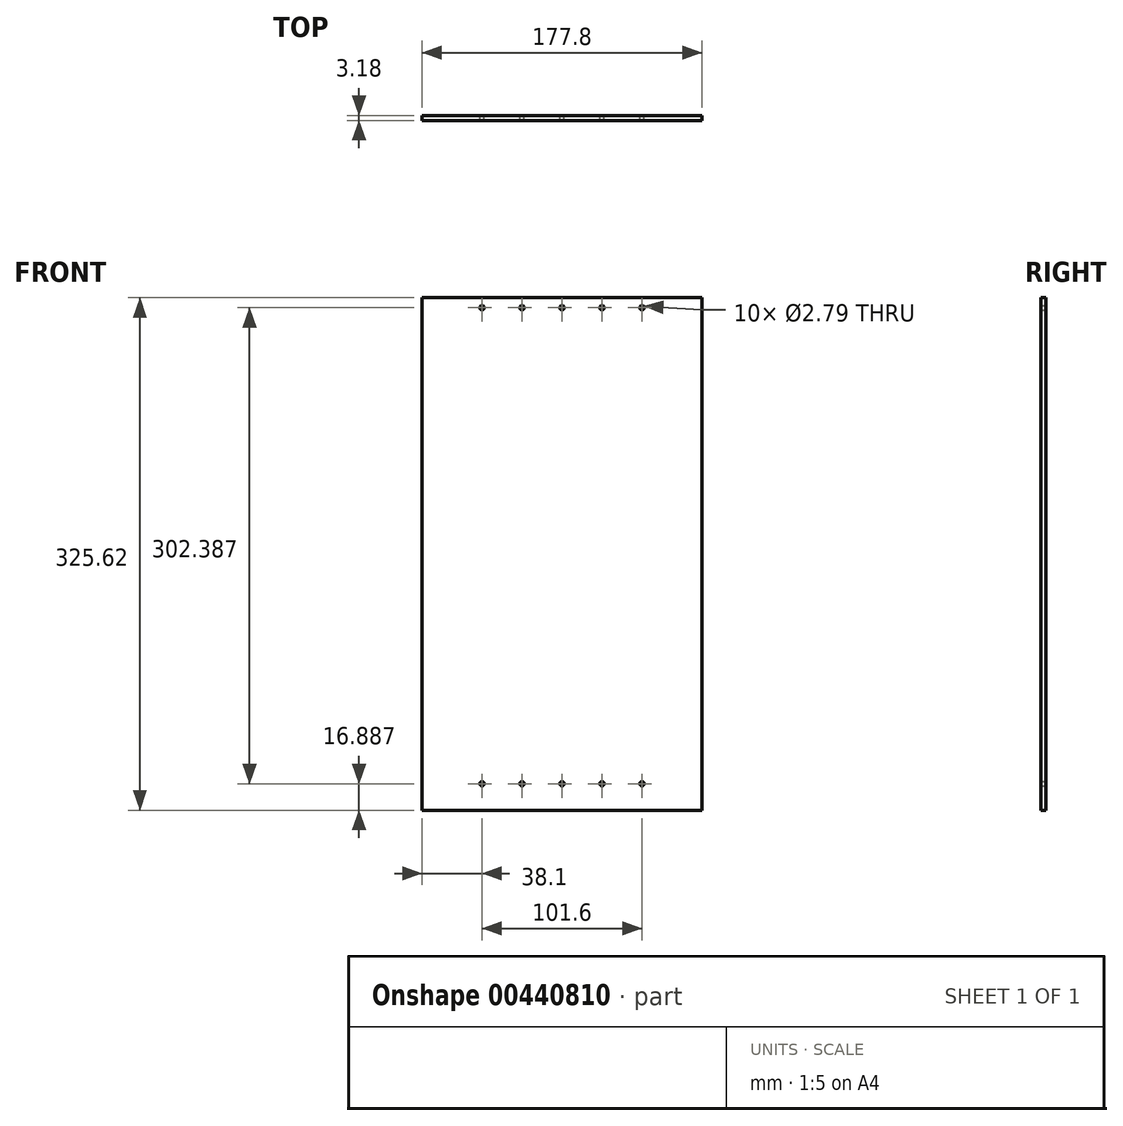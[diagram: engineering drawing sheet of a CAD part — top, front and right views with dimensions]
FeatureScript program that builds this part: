
annotation { "Feature Type Name" : "Feature", "Feature Type Description" : "" }
export const myFeature = defineFeature(function(context is Context, id is Id, definition is map)
    precondition{}
    {
        {
            var Q0;
            Q0=qCreatedBy(makeId("Front.planeOp"),FACE);
            var sketch = newSketch(context, id + "F0", { "sketchPlane" : qUnion([Q0])});
            skLineSegment(sketch, "E0.bottom", {"start": v(88.9, 162.81) * mm, "end": v(-88.9, 162.81) * mm});
            skLineSegment(sketch, "E0.top", {"start": v(88.9, -162.81) * mm, "end": v(-88.9, -162.81) * mm});
            skLineSegment(sketch, "E0.left", {"start": v(88.9, 162.81) * mm, "end": v(88.9, -162.81) * mm});
            skLineSegment(sketch, "E0.right", {"start": v(-88.9, 162.81) * mm, "end": v(-88.9, -162.81) * mm});
            skPoint(sketch, "E0.middle", {"position": v(0, 0) * mm});
            skLineSegment(sketch, "E1", {"start": v(0, 162.81) * mm, "end": v(0, 156.46) * mm});
            skCircle(sketch, "E2", {"center": v(0, 156.46) * mm, "radius": 1.4 * mm});
            skLineSegment(sketch, "E3", {"start": v(0, 156.46) * mm, "end": v(25.4, 156.46) * mm});
            skLineSegment(sketch, "E4", {"start": v(25.4, 156.46) * mm, "end": v(50.8, 156.46) * mm});
            skCircle(sketch, "E5", {"center": v(25.4, 156.46) * mm, "radius": 1.4 * mm});
            skCircle(sketch, "E6", {"center": v(50.8, 156.46) * mm, "radius": 1.4 * mm});
            skCircle(sketch, "E7.MirrorC", {"center": v(-50.8, 156.46) * mm, "radius": 1.4 * mm});
            skCircle(sketch, "E8.MirrorC", {"center": v(-25.4, 156.46) * mm, "radius": 1.4 * mm});
            skLineSegment(sketch, "E9", {"start": v(0, -162.81) * mm, "end": v(0, -145.92) * mm});
            skCircle(sketch, "E10", {"center": v(0, -145.92) * mm, "radius": 1.4 * mm});
            skLineSegment(sketch, "E11", {"start": v(0, -145.92) * mm, "end": v(25.4, -145.92) * mm});
            skLineSegment(sketch, "E12", {"start": v(25.4, -145.92) * mm, "end": v(50.8, -145.92) * mm});
            skCircle(sketch, "E13", {"center": v(50.8, -145.92) * mm, "radius": 1.4 * mm});
            skCircle(sketch, "E14", {"center": v(25.4, -145.92) * mm, "radius": 1.4 * mm});
            skCircle(sketch, "E15.MirrorC", {"center": v(-50.8, -145.92) * mm, "radius": 1.4 * mm});
            skCircle(sketch, "E16.MirrorC", {"center": v(-25.4, -145.92) * mm, "radius": 1.4 * mm});
            skSolve(sketch);
        }
        {
            var Q0;
            Q0 = qSketchRegion(id + "F0", true);
            extrude(context, id + "F1", {"entities" : qUnion([Q0]), "depth" : 3.17 * mm});
        }
    });
